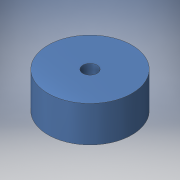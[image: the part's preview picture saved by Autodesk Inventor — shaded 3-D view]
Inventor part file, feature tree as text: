
AUTODESK INVENTOR PART (.ipt)
format: ipt  version: 2016 (Build 200138000, 138)  size: 94,208 bytes
history: native  units: in
note: dims shown in document units (in); Inventor stores cm internally (conversion verified against a paired STEP export)
features: extrude x1, sketch x1
ambient origin geometry x8: Origin, YZ Plane, XZ Plane, XY Plane, X Axis, Y Axis, Z Axis, Center Point
bodies: Solid1 (feature_tree)
feature tree (2):
  extrude  "Extrusion1"  Depth=0.3in
  sketch  "Sketch1"  dims[d0=0.7in d1=0.12in d2=0.3in d3=0.0in]
